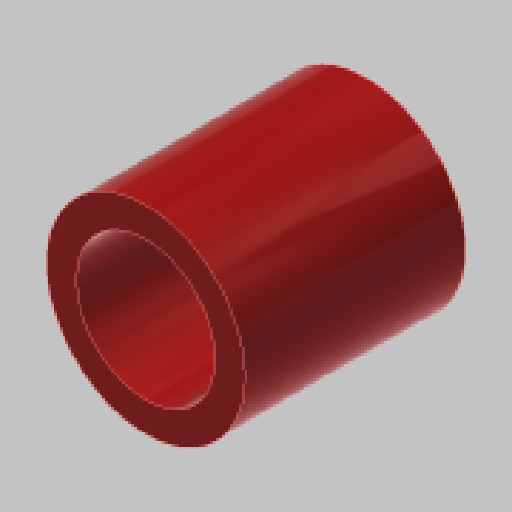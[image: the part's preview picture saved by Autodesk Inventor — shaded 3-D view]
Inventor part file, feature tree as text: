
AUTODESK INVENTOR PART (.ipt)
format: ipt  version: 2023.5 (Build 275446000, 446)  size: 120,320 bytes
history: native  units: in
note: dims shown in document units (in); Inventor stores cm internally (conversion verified against a paired STEP export)
features: extrude x1, sketch x1
ambient origin geometry x8: Origin, YZ Plane, XZ Plane, XY Plane, X Axis, Y Axis, Z Axis, Center Point
bodies: Solid1 (feature_tree)
feature tree (2):
  extrude  "Extrusion1"  Depth=0.928in
  sketch  "Sketch1"  dims[d0=0.585in d1=0.125in d2=0.928in d3=0.0in]
